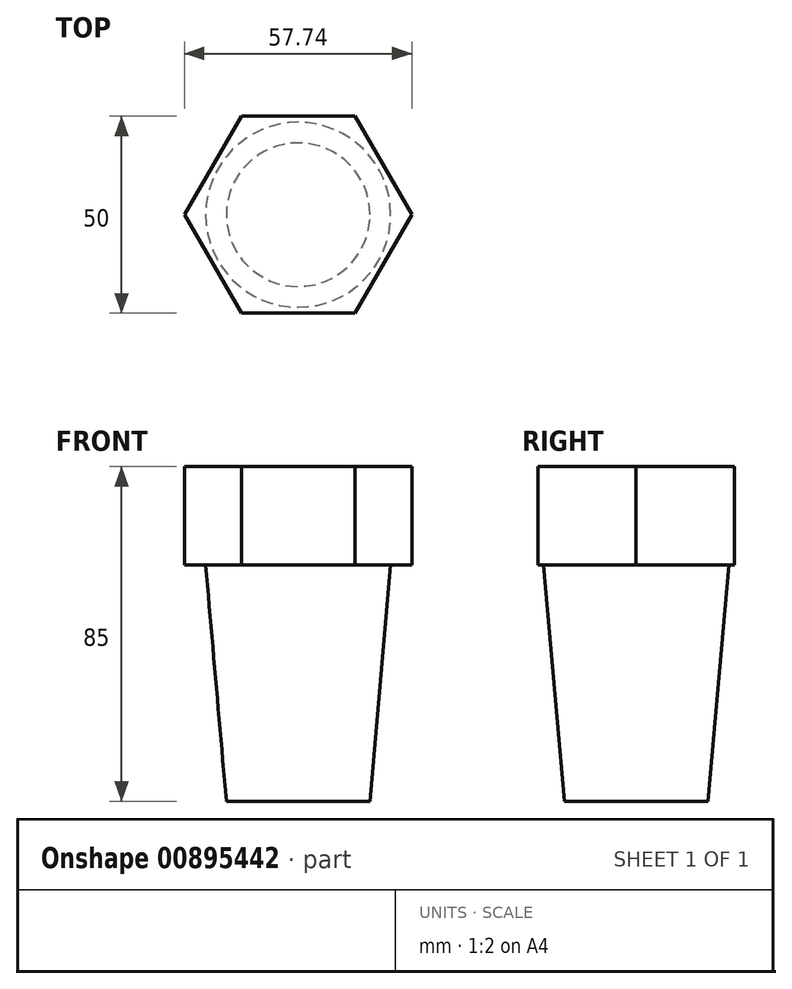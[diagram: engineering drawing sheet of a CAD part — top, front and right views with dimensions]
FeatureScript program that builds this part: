
annotation { "Feature Type Name" : "Feature", "Feature Type Description" : "" }
export const myFeature = defineFeature(function(context is Context, id is Id, definition is map)
    precondition{}
    {
        {
            var Q0;
            Q0=qCreatedBy(makeId("Front.planeOp"),FACE);
            var sketch = newSketch(context, id + "F0", { "sketchPlane" : qUnion([Q0])});
            skLineSegment(sketch, "E0", {"start": v(0, 0) * mm, "end": v(0, 145.25) * mm, "construction": true});
            skLineSegment(sketch, "E1", {"start": v(0, 0) * mm, "end": v(-18.25, 0) * mm});
            skLineSegment(sketch, "E2", {"start": v(-18.25, 0) * mm, "end": v(-23.5, 60) * mm});
            skLineSegment(sketch, "E3", {"start": v(-23.5, 60) * mm, "end": v(0, 60) * mm});
            skLineSegment(sketch, "E4", {"start": v(0, 60) * mm, "end": v(0, 0) * mm});
            skLineSegment(sketch, "E5", {"start": v(-20, 20) * mm, "end": v(0, 20) * mm, "construction": true});
            skLineSegment(sketch, "E6", {"start": v(0, 75) * mm, "end": v(0, 60) * mm});
            skSolve(sketch);
        }
        {
            var Q0;
            Q0 = qSketchRegion(id + "F0", true);
            var Q1;
            Q1=sQuery(id+"F0.wireOp",EDGE,"E0");
            revolve(context, id + "F1", {"surfaceOperationType" : NewSurfaceOperationType.NEW, "entities" : qUnion([Q0]), "axis" : qUnion([Q1]), "revolveType" : RevolveType.FULL});
        }
        {
            var Q0;
            Q0=makeQuery(id+"F1.opRevolve","SWEPT_FACE",FACE,{"disambiguationData":[OSD([sQuery(id+"F0.wireOp",EDGE,"E3")])]});
            var sketch = newSketch(context, id + "F2", { "sketchPlane" : qUnion([Q0])});
            skCircle(sketch, "E7", {"center": v(0, 0) * mm, "radius": 25 * mm, "construction": true});
            skLineSegment(sketch, "E8", {"start": v(-28.87, 0) * mm, "end": v(-14.43, 25) * mm});
            skLineSegment(sketch, "E9", {"start": v(-14.43, 25) * mm, "end": v(14.43, 25) * mm});
            skLineSegment(sketch, "E10", {"start": v(14.43, 25) * mm, "end": v(28.87, 0) * mm});
            skLineSegment(sketch, "E11", {"start": v(28.87, 0) * mm, "end": v(14.43, -25) * mm});
            skLineSegment(sketch, "E12", {"start": v(14.43, -25) * mm, "end": v(-14.43, -25) * mm});
            skLineSegment(sketch, "E13", {"start": v(-14.43, -25) * mm, "end": v(-28.87, 0) * mm});
            skLineSegment(sketch, "E14", {"start": v(-28.87, 0) * mm, "end": v(0, 0) * mm, "construction": true});
            skLineSegment(sketch, "E15", {"start": v(28.87, 0) * mm, "end": v(0, 0) * mm, "construction": true});
            skLineSegment(sketch, "E16", {"start": v(14.43, 25) * mm, "end": v(0, 0) * mm, "construction": true});
            skLineSegment(sketch, "E17", {"start": v(-14.43, 25) * mm, "end": v(0, 0) * mm, "construction": true});
            skLineSegment(sketch, "E18", {"start": v(14.43, -25) * mm, "end": v(0, 0) * mm, "construction": true});
            skLineSegment(sketch, "E19", {"start": v(-14.43, -25) * mm, "end": v(0, 0) * mm, "construction": true});
            skSolve(sketch);
        }
        {
            var Q0;
            Q0 = qSketchRegion(id + "F2", true);
            extrude(context, id + "F3", {"entities" : qUnion([Q0]), "operationType" : NewBodyOperationType.ADD, "depth" : 25 * mm, "offsetDistance" : 25 * mm});
        }
    });
